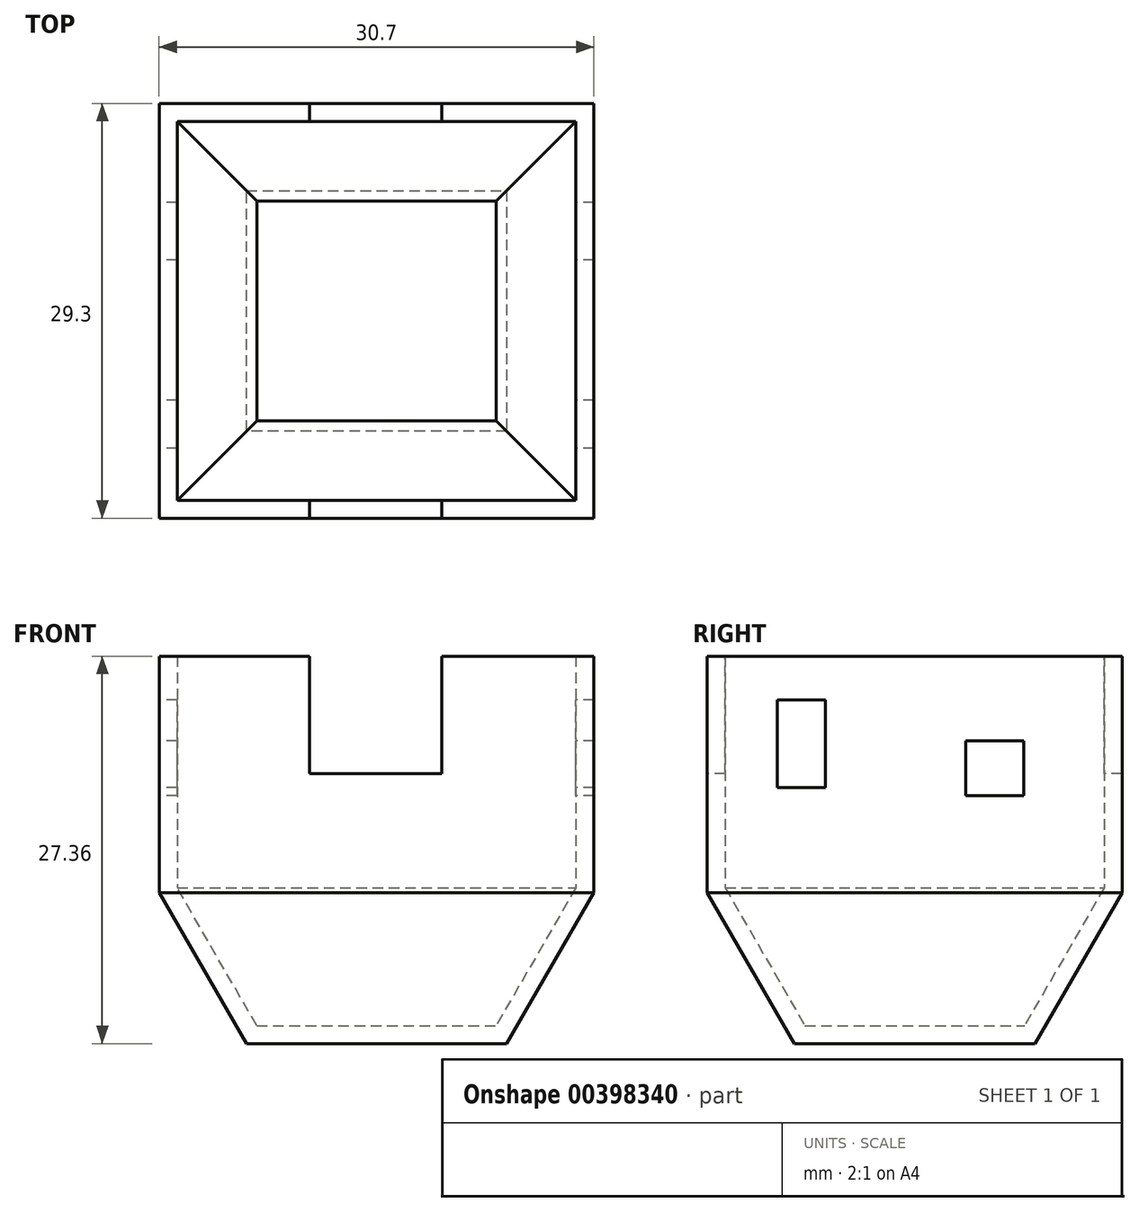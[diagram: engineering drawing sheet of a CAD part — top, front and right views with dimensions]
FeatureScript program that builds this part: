
annotation { "Feature Type Name" : "Feature", "Feature Type Description" : "" }
export const myFeature = defineFeature(function(context is Context, id is Id, definition is map)
    precondition{}
    {
        {
            var Q0;
            Q0=qCreatedBy(makeId("Top.planeOp"),FACE);
            var sketch = newSketch(context, id + "F0", { "sketchPlane" : qUnion([Q0])});
            skLineSegment(sketch, "E0.bottom", {"start": v(-43.75, 39.72) * mm, "end": v(43.75, 39.72) * mm});
            skLineSegment(sketch, "E0.top", {"start": v(-43.75, -41.16) * mm, "end": v(43.75, -41.16) * mm});
            skLineSegment(sketch, "E0.left", {"start": v(-43.75, 39.72) * mm, "end": v(-43.75, -41.16) * mm});
            skLineSegment(sketch, "E0.right", {"start": v(43.75, 39.72) * mm, "end": v(43.75, -41.16) * mm});
            skSolve(sketch);
        }
        {
            var Q0;
            Q0 = qSketchRegion(id + "F0", true);
            extrude(context, id + "F1", {"entities" : qUnion([Q0]), "depth" : 50.8 * mm, "hasDraft" : true, "draftAngle" : 30 * degree});
        }
        {
            var Q0;
            Q0=makeQuery(id+"F1.opExtrude","CAP_FACE",FACE,{"disambiguationData":[OSD([sQuery(id+"F0.wireOp",EDGE,"E0.bottom"),sQuery(id+"F0.wireOp",EDGE,"E0.top"),sQuery(id+"F0.wireOp",EDGE,"E0.left"),sQuery(id+"F0.wireOp",EDGE,"E0.right")])],"isStart":false});
            var sketch = newSketch(context, id + "F2", { "sketchPlane" : qUnion([Q0])});
            skSolve(sketch);
        }
        {
            var Q0;
            Q0=makeQuery(id+"F2.imprint","IMPRINT",FACE,{"disambiguationData":[TD([[makeQuery(id+"F2.imprint","IMPRINT",EDGE,{"derivedFrom":makeQuery(id+"F1.opExtrude","CAP_EDGE",EDGE,{"disambiguationData":[OSD([sQuery(id+"F0.wireOp",EDGE,"E0.bottom")])],"isStart":false})}),-1.0]])]});
            var sketch = newSketch(context, id + "F3", { "sketchPlane" : qUnion([Q0])});
            skLineSegment(sketch, "E1.bottom", {"start": v(-43.46, 43.17) * mm, "end": v(45.47, 43.17) * mm});
            skLineSegment(sketch, "E1.top", {"start": v(-43.46, -46.05) * mm, "end": v(45.47, -46.05) * mm});
            skLineSegment(sketch, "E1.left", {"start": v(-43.46, 43.17) * mm, "end": v(-43.46, -46.05) * mm});
            skLineSegment(sketch, "E1.right", {"start": v(45.47, 43.17) * mm, "end": v(45.47, -46.05) * mm});
            skSolve(sketch);
        }
        {
            var Q0;
            Q0 = qSketchRegion(id + "F3", true);
            var Q1;
            Q1=makeQuery(id+"F2.imprint","IMPRINT",FACE,{"disambiguationData":[TD([[makeQuery(id+"F2.imprint","IMPRINT",EDGE,{"derivedFrom":makeQuery(id+"F1.opExtrude","CAP_EDGE",EDGE,{"disambiguationData":[OSD([sQuery(id+"F0.wireOp",EDGE,"E0.bottom")])],"isStart":false})}),-1.0]])]});
            extrude(context, id + "F4", {"entities" : qUnion([Q0, Q1]), "operationType" : NewBodyOperationType.ADD, "depth" : 79.5 * mm});
        }
        {
            var Q0;
            Q0=makeQuery(id+"F1.opExtrude","CAP_FACE",FACE,{"disambiguationData":[OSD([sQuery(id+"F0.wireOp",EDGE,"E0.bottom"),sQuery(id+"F0.wireOp",EDGE,"E0.top"),sQuery(id+"F0.wireOp",EDGE,"E0.left"),sQuery(id+"F0.wireOp",EDGE,"E0.right")])],"isStart":true});
            var sketch = newSketch(context, id + "F5", { "sketchPlane" : qUnion([Q0])});
            skLineSegment(sketch, "E2.bottom", {"start": v(0, 41.16) * mm, "end": v(-43.75, 41.16) * mm});
            skLineSegment(sketch, "E2.top", {"start": v(0, 0) * mm, "end": v(-43.75, 0) * mm});
            skLineSegment(sketch, "E2.left", {"start": v(0, 41.16) * mm, "end": v(0, 0) * mm});
            skLineSegment(sketch, "E2.right", {"start": v(-43.75, 41.16) * mm, "end": v(-43.75, 0) * mm});
            skSolve(sketch);
        }
        {
            var Q0;
            Q0=makeQuery(id+"F1.opExtrude","SWEPT_BODY",BODY,{"disambiguationData":[OSD([sQuery(id+"F0.wireOp",EDGE,"E0.bottom"),sQuery(id+"F0.wireOp",EDGE,"E0.top"),sQuery(id+"F0.wireOp",EDGE,"E0.left"),sQuery(id+"F0.wireOp",EDGE,"E0.right")])]});
            var Q1;
            Q1=sQuery(id+"F5.wireOp",VERTEX,"E2.left.end");
            transform(context, id + "F6", {"entities" : qUnion([Q0]), "transformType" : TransformType.SCALE_UNIFORMLY, "scale" : .21, "scalePoint" : qUnion([Q1]), "makeCopy" : false});
        }
        {
            var Q0;
            Q0=makeQuery(id+"F4.opExtrude","CAP_FACE",FACE,{"disambiguationData":[OSD([sQuery(id+"F0.wireOp",EDGE,"E0.bottom"),sQuery(id+"F0.wireOp",EDGE,"E0.top"),sQuery(id+"F0.wireOp",EDGE,"E0.left"),sQuery(id+"F0.wireOp",EDGE,"E0.right")])],"isStart":false});
            shell(context, id + "F7", {"entities" : qUnion([Q0]), "thickness" : 1.27 * mm});
        }
        {
            var Q0;
            Q0=makeQuery(id+"F4.opExtrude","SWEPT_FACE",FACE,{"disambiguationData":[OSD([sQuery(id+"F0.wireOp",EDGE,"E0.top")])]});
            var sketch = newSketch(context, id + "F8", { "sketchPlane" : qUnion([Q0])});
            skLineSegment(sketch, "E3.bottom", {"start": v(-4.73, 27.36) * mm, "end": v(0, 27.36) * mm});
            skLineSegment(sketch, "E3.top", {"start": v(-4.73, 19.05) * mm, "end": v(0, 19.05) * mm});
            skLineSegment(sketch, "E3.left", {"start": v(-4.73, 27.36) * mm, "end": v(-4.73, 19.05) * mm});
            skLineSegment(sketch, "E3.right", {"start": v(0, 27.36) * mm, "end": v(0, 19.05) * mm});
            skLineSegment(sketch, "E4.bottom", {"start": v(0, 19.05) * mm, "end": v(4.6, 19.05) * mm});
            skLineSegment(sketch, "E4.top", {"start": v(0, 27.36) * mm, "end": v(4.6, 27.36) * mm});
            skLineSegment(sketch, "E4.left", {"start": v(0, 19.05) * mm, "end": v(0, 27.36) * mm});
            skLineSegment(sketch, "E4.right", {"start": v(4.6, 19.05) * mm, "end": v(4.6, 27.36) * mm});
            skSolve(sketch);
        }
        {
            var Q0;
            Q0=makeQuery(id+"F8.imprint","IMPRINT",FACE,{"disambiguationData":[TD([[makeQuery(id+"F8.imprint","IMPRINT",EDGE,{"derivedFrom":sQuery(id+"F8.wireOp",EDGE,"E3.bottom")}),-1.0]])]});
            var Q1;
            Q1=makeQuery(id+"F8.imprint","IMPRINT",FACE,{"disambiguationData":[TD([[makeQuery(id+"F8.imprint","IMPRINT",EDGE,{"derivedFrom":sQuery(id+"F8.wireOp",EDGE,"E4.bottom")}),1.0]])]});
            extrude(context, id + "F9", {"entities" : qUnion([Q0, Q1]), "operationType" : NewBodyOperationType.REMOVE, "endBound" : BoundingType.THROUGH_ALL, "oppositeDirection" : true, "depth" : 25.4 * mm});
        }
        {
            var Q0;
            Q0=makeQuery(id+"F4.opExtrude","SWEPT_FACE",FACE,{"disambiguationData":[OSD([sQuery(id+"F0.wireOp",EDGE,"E0.left")])]});
            var sketch = newSketch(context, id + "F10", { "sketchPlane" : qUnion([Q0])});
            skLineSegment(sketch, "E5.bottom", {"start": v(-7.53, 21.4) * mm, "end": v(-3.45, 21.4) * mm});
            skLineSegment(sketch, "E5.top", {"start": v(-7.53, 17.51) * mm, "end": v(-3.45, 17.51) * mm});
            skLineSegment(sketch, "E5.left", {"start": v(-7.53, 21.4) * mm, "end": v(-7.53, 17.51) * mm});
            skLineSegment(sketch, "E5.right", {"start": v(-3.45, 21.4) * mm, "end": v(-3.45, 17.51) * mm});
            skLineSegment(sketch, "E6.bottom", {"start": v(6.47, 24.29) * mm, "end": v(9.86, 24.29) * mm});
            skLineSegment(sketch, "E6.top", {"start": v(6.47, 18.08) * mm, "end": v(9.86, 18.08) * mm});
            skLineSegment(sketch, "E6.left", {"start": v(6.47, 24.29) * mm, "end": v(6.47, 18.08) * mm});
            skLineSegment(sketch, "E6.right", {"start": v(9.86, 24.29) * mm, "end": v(9.86, 18.08) * mm});
            skSolve(sketch);
        }
        {
            var Q0;
            Q0=makeQuery(id+"F10.imprint","IMPRINT",FACE,{"disambiguationData":[TD([[makeQuery(id+"F10.imprint","IMPRINT",EDGE,{"derivedFrom":sQuery(id+"F10.wireOp",EDGE,"E6.bottom")}),-1.0]])]});
            var Q1;
            Q1=makeQuery(id+"F10.imprint","IMPRINT",FACE,{"disambiguationData":[TD([[makeQuery(id+"F10.imprint","IMPRINT",EDGE,{"derivedFrom":sQuery(id+"F10.wireOp",EDGE,"E5.bottom")}),-1.0]])]});
            extrude(context, id + "F11", {"entities" : qUnion([Q0, Q1]), "operationType" : NewBodyOperationType.REMOVE, "endBound" : BoundingType.THROUGH_ALL, "oppositeDirection" : true, "depth" : 25.4 * mm});
        }
    });
